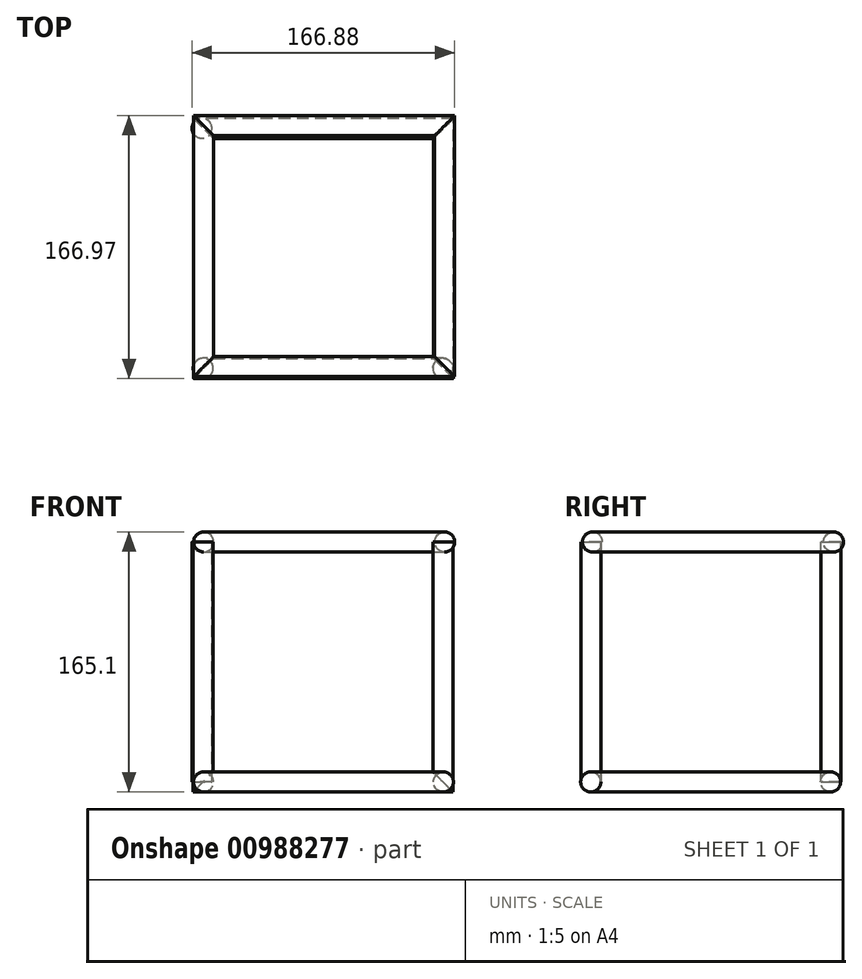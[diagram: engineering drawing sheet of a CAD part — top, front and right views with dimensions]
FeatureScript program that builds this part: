
annotation { "Feature Type Name" : "Feature", "Feature Type Description" : "" }
export const myFeature = defineFeature(function(context is Context, id is Id, definition is map)
    precondition{}
    {
        {
            var Q0;
            Q0=qCreatedBy(makeId("Top.planeOp"),FACE);
            var sketch = newSketch(context, id + "F0", { "sketchPlane" : qUnion([Q0])});
            skLineSegment(sketch, "E0.bottom", {"start": v(-76.37, 76.03) * mm, "end": v(76.03, 76.03) * mm});
            skLineSegment(sketch, "E0.top", {"start": v(-76.37, -76.37) * mm, "end": v(76.03, -76.37) * mm});
            skLineSegment(sketch, "E0.left", {"start": v(-76.37, 76.03) * mm, "end": v(-76.37, -76.37) * mm});
            skLineSegment(sketch, "E0.right", {"start": v(76.03, 76.03) * mm, "end": v(76.03, -76.37) * mm});
            skSolve(sketch);
        }
        {
            var Q0;
            Q0=qCreatedBy(makeId("Front.planeOp"),FACE);
            var sketch = newSketch(context, id + "F1", { "sketchPlane" : qUnion([Q0])});
            skCircle(sketch, "E1", {"center": v(-76.37, 0) * mm, "radius": 6.35 * mm});
            skSolve(sketch);
        }
        {
            var Q0;
            Q0 = qSketchRegion(id + "F1", true);
            var Q1;
            Q1 = qConstructionFilter(qBodyType(qCreatedBy(id + "F0" ,EDGE), BodyType.WIRE), ConstructionObject.NO);
            sweep(context, id + "F2", {"profiles" : qUnion([Q0]), "path" : qUnion([Q1])});
        }
        {
            var Q0;
            Q0=qCreatedBy(makeId("Front.planeOp"),FACE);
            cPlane(context, id + "F3", {"entities" : qUnion([Q0]), "cplaneType" : CPlaneType.OFFSET, "offset" : 76.2 * mm, "oppositeDirection" : true, "width" : 152.4 * mm, "height" : 152.4 * mm});
        }
        {
            var Q0;
            Q0=qCreatedBy(makeId("Front.planeOp"),FACE);
            cPlane(context, id + "F4", {"entities" : qUnion([Q0]), "cplaneType" : CPlaneType.OFFSET, "offset" : 76.2 * mm, "width" : 152.4 * mm, "height" : 152.4 * mm});
        }
        {
            var Q0;
            Q0=qCreatedBy(id+"F3.planeOp",FACE);
            var sketch = newSketch(context, id + "F5", { "sketchPlane" : qUnion([Q0])});
            skLineSegment(sketch, "E2", {"start": v(-77.37, 0) * mm, "end": v(-77.37, 152.4) * mm});
            skLineSegment(sketch, "E3", {"start": v(76.03, 0) * mm, "end": v(76.03, 152.4) * mm, "construction": true});
            skSolve(sketch);
        }
        {
            var Q0;
            Q0=qCreatedBy(makeId("Top.planeOp"),FACE);
            var sketch = newSketch(context, id + "F6", { "sketchPlane" : qUnion([Q0])});
            skCircle(sketch, "E4", {"center": v(-77.37, 76.2) * mm, "radius": 6.35 * mm});
            skSolve(sketch);
        }
        {
            var Q0;
            Q0 = qSketchRegion(id + "F6", true);
            var Q1;
            Q1 = qConstructionFilter(qBodyType(qCreatedBy(id + "F5" ,EDGE), BodyType.WIRE), ConstructionObject.NO);
            sweep(context, id + "F7", {"profiles" : qUnion([Q0]), "path" : qUnion([Q1])});
        }
        {
            var Q0;
            Q0=qCreatedBy(id+"F4.planeOp",FACE);
            var sketch = newSketch(context, id + "F8", { "sketchPlane" : qUnion([Q0])});
            skLineSegment(sketch, "E5", {"start": v(-76.6, 0) * mm, "end": v(-76.6, 152.4) * mm});
            skLineSegment(sketch, "E6", {"start": v(75.69, 0) * mm, "end": v(75.69, 152.4) * mm});
            skLineSegment(sketch, "E7", {"start": v(-76.6, 0) * mm, "end": v(75.69, 0) * mm});
            skSolve(sketch);
        }
        {
            var Q0;
            Q0=qCreatedBy(makeId("Top.planeOp"),FACE);
            var sketch = newSketch(context, id + "F9", { "sketchPlane" : qUnion([Q0])});
            skCircle(sketch, "E8", {"center": v(-76.6, -76.2) * mm, "radius": 6.35 * mm});
            skSolve(sketch);
        }
        {
            var Q0;
            Q0 = qSketchRegion(id + "F9", true);
            var Q1;
            Q1 = qConstructionFilter(qBodyType(qCreatedBy(id + "F8" ,EDGE), BodyType.WIRE), ConstructionObject.NO);
            sweep(context, id + "F10", {"profiles" : qUnion([Q0]), "path" : qUnion([Q1])});
        }
        {
            var Q0;
            Q0=qCreatedBy(makeId("Top.planeOp"),FACE);
            cPlane(context, id + "F11", {"entities" : qUnion([Q0]), "cplaneType" : CPlaneType.OFFSET, "offset" : 152.4 * mm, "width" : 152.4 * mm, "height" : 152.4 * mm});
        }
        {
            var Q0;
            Q0=qCreatedBy(id+"F11.planeOp",FACE);
            var sketch = newSketch(context, id + "F12", { "sketchPlane" : qUnion([Q0])});
            skLineSegment(sketch, "E9.bottom", {"start": v(-76.29, -75.2) * mm, "end": v(76.81, -75.2) * mm});
            skLineSegment(sketch, "E9.top", {"start": v(-76.29, 77.9) * mm, "end": v(76.81, 77.9) * mm});
            skLineSegment(sketch, "E9.left", {"start": v(-76.29, -75.2) * mm, "end": v(-76.29, 77.9) * mm});
            skLineSegment(sketch, "E9.right", {"start": v(76.81, -75.2) * mm, "end": v(76.81, 77.9) * mm});
            skSolve(sketch);
        }
        {
            var Q0;
            Q0=qCreatedBy(id+"F3.planeOp",FACE);
            var sketch = newSketch(context, id + "F13", { "sketchPlane" : qUnion([Q0])});
            skCircle(sketch, "E10", {"center": v(-76.29, 152.4) * mm, "radius": 6.35 * mm});
            skSolve(sketch);
        }
        {
            var Q0;
            Q0 = qSketchRegion(id + "F13", true);
            var Q1;
            Q1 = qConstructionFilter(qBodyType(qCreatedBy(id + "F12" ,EDGE), BodyType.WIRE), ConstructionObject.NO);
            sweep(context, id + "F14", {"profiles" : qUnion([Q0]), "path" : qUnion([Q1])});
        }
    });
